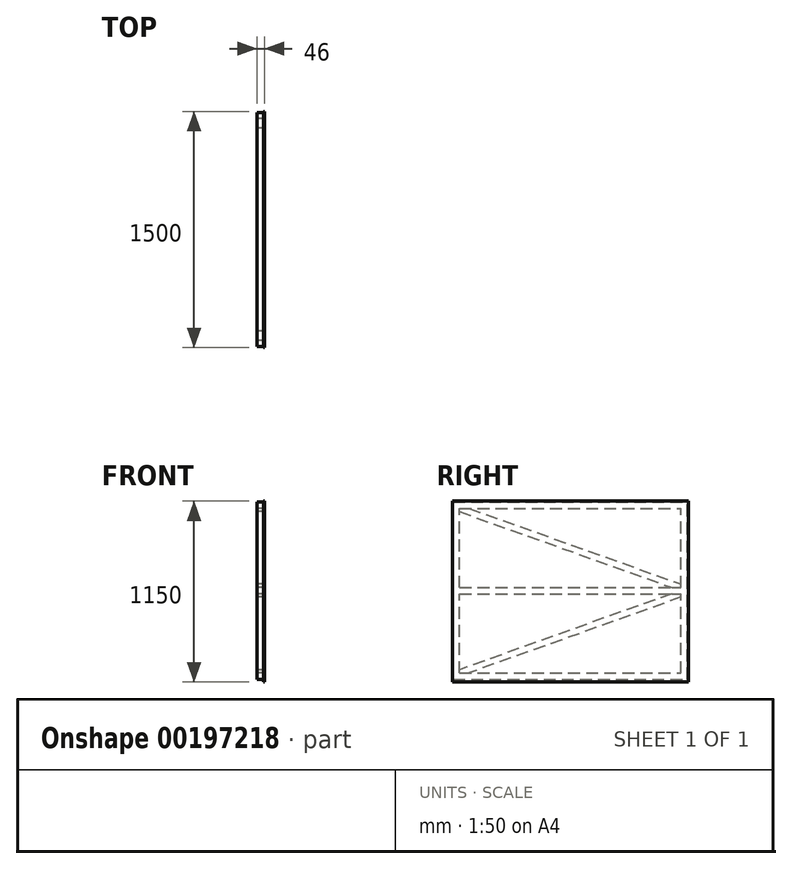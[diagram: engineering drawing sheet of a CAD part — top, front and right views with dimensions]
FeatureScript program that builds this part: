
annotation { "Feature Type Name" : "Feature", "Feature Type Description" : "" }
export const myFeature = defineFeature(function(context is Context, id is Id, definition is map)
    precondition{}
    {
        {
            var Q0;
            Q0=qCreatedBy(makeId("Right.planeOp"),FACE);
            var sketch = newSketch(context, id + "F0", { "sketchPlane" : qUnion([Q0])});
            skLineSegment(sketch, "E0.bottom", {"start": v(750, 575) * mm, "end": v(-750, 575) * mm});
            skLineSegment(sketch, "E0.top", {"start": v(750, -575) * mm, "end": v(-750, -575) * mm});
            skLineSegment(sketch, "E0.left", {"start": v(750, 575) * mm, "end": v(750, -575) * mm});
            skLineSegment(sketch, "E0.right", {"start": v(-750, 575) * mm, "end": v(-750, -575) * mm});
            skPoint(sketch, "E0.middle", {"position": v(0, 0) * mm});
            skSolve(sketch);
        }
        {
            var Q0;
            Q0=qSketchRegion(id+"F0",true);
            extrude(context, id + "F1", {"entities" : qUnion([Q0]), "depth" : 6 * mm});
        }
        {
            var Q0;
            Q0=qCreatedBy(makeId("Front.planeOp"),FACE);
            var sketch = newSketch(context, id + "F2", { "sketchPlane" : qUnion([Q0])});
            skLineSegment(sketch, "E1.bottom", {"start": v(0, 569) * mm, "end": v(-40, 569) * mm});
            skLineSegment(sketch, "E1.top", {"start": v(0, 529) * mm, "end": v(-40, 529) * mm});
            skLineSegment(sketch, "E1.left", {"start": v(0, 569) * mm, "end": v(0, 529) * mm});
            skLineSegment(sketch, "E1.right", {"start": v(-40, 569) * mm, "end": v(-40, 529) * mm});
            skLineSegment(sketch, "E2.0.1.0", {"start": v(0, 26) * mm, "end": v(-40, 26) * mm});
            skLineSegment(sketch, "E2.0.1.1", {"start": v(-40, 26) * mm, "end": v(-40, -14) * mm});
            skLineSegment(sketch, "E2.0.1.2", {"start": v(0, 26) * mm, "end": v(0, -14) * mm});
            skLineSegment(sketch, "E2.0.1.3", {"start": v(0, -14) * mm, "end": v(-40, -14) * mm});
            skLineSegment(sketch, "E2.direction1", {"start": v(-40, 569) * mm, "end": v(-15, 569) * mm, "construction": true});
            skLineSegment(sketch, "E2.direction2", {"start": v(-40, 569) * mm, "end": v(-40, 26) * mm, "construction": true});
            skLineSegment(sketch, "E3.0.0.2", {"start": v(0, -517) * mm, "end": v(-40, -517) * mm});
            skLineSegment(sketch, "E3.3.0.2", {"start": v(-40, -517) * mm, "end": v(-40, -557) * mm});
            skLineSegment(sketch, "E3.6.0.2", {"start": v(0, -517) * mm, "end": v(0, -557) * mm});
            skLineSegment(sketch, "E3.9.0.2", {"start": v(0, -557) * mm, "end": v(-40, -557) * mm});
            skSolve(sketch);
        }
        {
            var Q0;
            Q0=qSketchRegion(id+"F2",true);
            extrude(context, id + "F3", {"entities" : qUnion([Q0]), "operationType" : NewBodyOperationType.ADD, "endBound" : BoundingType.SYMMETRIC, "depth" : 1408 * mm});
        }
        {
            var Q0;
            Q0=makeQuery(id+"F3.opExtrude","SWEPT_FACE",FACE,{"disambiguationData":[OSD([sQuery(id+"F2.wireOp",EDGE,"E1.bottom")])]});
            var sketch = newSketch(context, id + "F4", { "sketchPlane" : qUnion([Q0])});
            skLineSegment(sketch, "E4.bottom", {"start": v(0, -704) * mm, "end": v(-40, -704) * mm});
            skLineSegment(sketch, "E4.top", {"start": v(0, -744) * mm, "end": v(-40, -744) * mm});
            skLineSegment(sketch, "E4.left", {"start": v(0, -704) * mm, "end": v(0, -744) * mm});
            skLineSegment(sketch, "E4.right", {"start": v(-40, -704) * mm, "end": v(-40, -744) * mm});
            skLineSegment(sketch, "E5.bottom", {"start": v(0, 704) * mm, "end": v(-40, 704) * mm});
            skLineSegment(sketch, "E5.top", {"start": v(0, 744) * mm, "end": v(-40, 744) * mm});
            skLineSegment(sketch, "E5.left", {"start": v(0, 704) * mm, "end": v(0, 744) * mm});
            skLineSegment(sketch, "E5.right", {"start": v(-40, 704) * mm, "end": v(-40, 744) * mm});
            skSolve(sketch);
        }
        {
            var Q0;
            Q0=qSketchRegion(id+"F4",true);
            extrude(context, id + "F5", {"entities" : qUnion([Q0]), "operationType" : NewBodyOperationType.ADD, "oppositeDirection" : true, "depth" : 1126 * mm});
        }
        {
            var Q0;
            Q0=makeQuery(id+"F5.boolean.opBoolean","MERGE",FACE,{"derivedFrom":[makeQuery(id+"F3.opExtrude","SWEPT_FACE",FACE,{"disambiguationData":[OSD([sQuery(id+"F2.wireOp",EDGE,"E1.right")])]}),makeQuery(id+"F3.opExtrude","SWEPT_FACE",FACE,{"disambiguationData":[OSD([sQuery(id+"F2.wireOp",EDGE,"E2.0.1.1")])]}),makeQuery(id+"F3.opExtrude","SWEPT_FACE",FACE,{"disambiguationData":[OSD([sQuery(id+"F2.wireOp",EDGE,"E3.3.0.2")])]}),makeQuery(id+"F5.opExtrude","SWEPT_FACE",FACE,{"disambiguationData":[OSD([sQuery(id+"F4.wireOp",EDGE,"E4.right")])]}),makeQuery(id+"F5.opExtrude","SWEPT_FACE",FACE,{"disambiguationData":[OSD([sQuery(id+"F4.wireOp",EDGE,"E5.right")])]})]});
            var sketch = newSketch(context, id + "F6", { "sketchPlane" : qUnion([Q0])});
            skLineSegment(sketch, "E6.0", {"start": v(644.55, 529) * mm, "end": v(-704, 47.24) * mm});
            skLineSegment(sketch, "E7.0", {"start": v(704, 507.76) * mm, "end": v(-644.55, 26) * mm});
            skLineSegment(sketch, "E8.0", {"start": v(-704, -35.24) * mm, "end": v(644.55, -517) * mm});
            skLineSegment(sketch, "E9.0", {"start": v(-644.55, -14) * mm, "end": v(704, -495.76) * mm});
            skLineSegment(sketch, "E10", {"start": v(-704, 47.24) * mm, "end": v(-704, 26) * mm});
            skLineSegment(sketch, "E11", {"start": v(644.55, 529) * mm, "end": v(704, 529) * mm});
            skLineSegment(sketch, "E12", {"start": v(704, -495.76) * mm, "end": v(704, -517) * mm});
            skLineSegment(sketch, "E13", {"start": v(-704, -35.24) * mm, "end": v(-704, -14) * mm});
            skLineSegment(sketch, "E14", {"start": v(-704, 26) * mm, "end": v(-644.55, 26) * mm});
            skLineSegment(sketch, "E15", {"start": v(-704, -14) * mm, "end": v(-644.55, -14) * mm});
            skLineSegment(sketch, "E16", {"start": v(704, -517) * mm, "end": v(644.55, -517) * mm});
            skLineSegment(sketch, "E17", {"start": v(704, 507.76) * mm, "end": v(704, 529) * mm});
            skSolve(sketch);
        }
        {
            var Q0;
            Q0=qSketchRegion(id+"F6",true);
            extrude(context, id + "F7", {"entities" : qUnion([Q0]), "oppositeDirection" : true, "depth" : 40 * mm});
        }
    });
